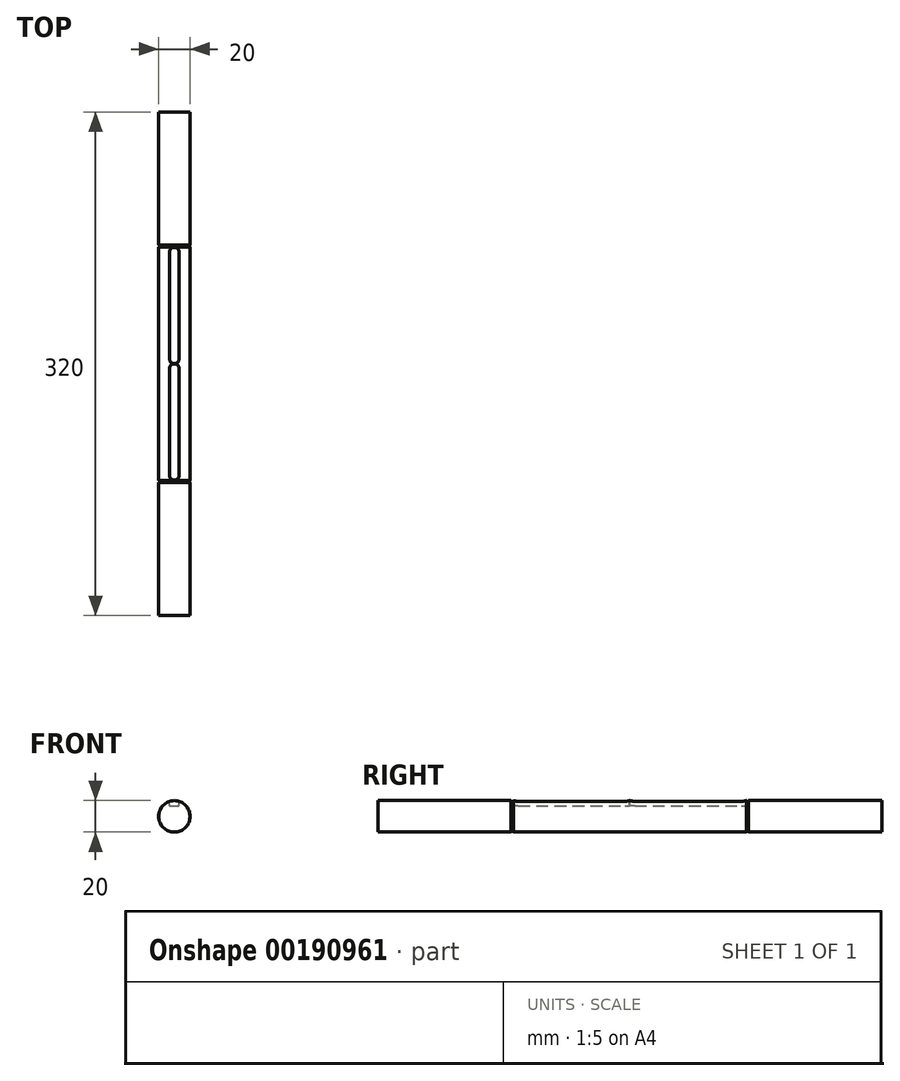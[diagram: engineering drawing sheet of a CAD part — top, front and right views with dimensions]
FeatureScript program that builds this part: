
annotation { "Feature Type Name" : "Feature", "Feature Type Description" : "" }
export const myFeature = defineFeature(function(context is Context, id is Id, definition is map)
    precondition{}
    {
        {
            var Q0;
            Q0=qCreatedBy(makeId("Front.planeOp"),FACE);
            var sketch = newSketch(context, id + "F0", { "sketchPlane" : qUnion([Q0])});
            skCircle(sketch, "E0", {"center": v(0, 0) * mm, "radius": 10 * mm});
            skSolve(sketch);
        }
        {
            var Q0;
            Q0=makeQuery(id+"F0.imprint","IMPRINT",FACE,{"disambiguationData":[TD([[makeQuery(id+"F0.imprint","IMPRINT",EDGE,{"derivedFrom":sQuery(id+"F0.wireOp",EDGE,"E0")}),1.0]])]});
            extrude(context, id + "F1", {"entities" : qUnion([Q0]), "depth" : 320 * mm});
        }
        {
            var Q0;
            Q0=qCreatedBy(makeId("Top.planeOp"),FACE);
            cPlane(context, id + "F2", {"entities" : qUnion([Q0]), "cplaneType" : CPlaneType.OFFSET, "offset" : 12.5 * mm, "width" : 150 * mm, "height" : 150 * mm});
        }
        {
            var Q0;
            Q0=qCreatedBy(id+"F2.planeOp",FACE);
            var sketch = newSketch(context, id + "F3", { "sketchPlane" : qUnion([Q0])});
            skLineSegment(sketch, "E1.bottom", {"start": v(-3, -230.9) * mm, "end": v(3, -230.9) * mm});
            skLineSegment(sketch, "E1.top", {"start": v(-3, -89.1) * mm, "end": v(3, -89.1) * mm});
            skLineSegment(sketch, "E1.left", {"start": v(-3, -230.9) * mm, "end": v(-3, -89.1) * mm});
            skLineSegment(sketch, "E1.right", {"start": v(3, -230.9) * mm, "end": v(3, -89.1) * mm});
            skArc(sketch, "E2", {"start": v(-3, -89.1) * mm, "mid": v(0, -86.1) * mm, "end": v(3, -89.1) * mm});
            skArc(sketch, "E3", {"start": v(3, -230.9) * mm, "mid": v(0, -233.9) * mm, "end": v(-3, -230.9) * mm});
            skCircle(sketch, "E4", {"center": v(0, -156.9) * mm, "radius": 3 * mm});
            skCircle(sketch, "E5", {"center": v(0, -163.1) * mm, "radius": 3 * mm});
            skSolve(sketch);
        }
        {
            var Q0;
            Q0=makeQuery(id+"F3.imprint","IMPRINT",FACE,{"disambiguationData":[TD([[makeQuery(id+"F3.imprint","IMPRINT",EDGE,{"derivedFrom":sQuery(id+"F3.wireOp",EDGE,"E1.bottom")}),1.0]])]});
            var Q1;
            Q1=makeQuery(id+"F3.imprint","IMPRINT",FACE,{"disambiguationData":[TD([[makeQuery(id+"F3.imprint","IMPRINT",EDGE,{"derivedFrom":sQuery(id+"F3.wireOp",EDGE,"E1.top")}),1.0]])]});
            var Q2;
            Q2=makeQuery(id+"F3.imprint","IMPRINT",FACE,{"disambiguationData":[TD([[makeQuery(id+"F3.imprint","IMPRINT",EDGE,{"derivedFrom":sQuery(id+"F3.wireOp",EDGE,"E1.bottom")}),-1.0]])]});
            var Q3;
            {var subQ0=sQuery(id+"F3.wireOp",EDGE,"E1.top");Q3=makeQuery(id+"F3.imprint","IMPRINT",FACE,{"disambiguationData":[TD([[makeQuery(id+"F3.imprint","IMPRINT",EDGE,{"derivedFrom":subQ0}),-1.0]])]});}
            var Q4;
            {var subQ0=sQuery(id+"F3.wireOp",EDGE,"E4");var subQ1=makeQuery(id+"F3.imprint","INTERSECT",VERTEX,{"derivedFrom":[sQuery(id+"F3.wireOp",EDGE,"E1.left"),subQ0]});Q4=makeQuery(id+"F3.imprint","IMPRINT",FACE,{"disambiguationData":[TD([[makeQuery(id+"F3.imprint","IMPRINT",EDGE,{"disambiguationData":[TD([[subQ1,1.0]])],"derivedFrom":subQ0}),1.0]])]});}
            var Q5;
            {var subQ0=sQuery(id+"F3.wireOp",EDGE,"E5");var subQ1=makeQuery(id+"F3.imprint","INTERSECT",VERTEX,{"derivedFrom":[sQuery(id+"F3.wireOp",EDGE,"E1.right"),subQ0]});Q5=makeQuery(id+"F3.imprint","IMPRINT",FACE,{"disambiguationData":[TD([[makeQuery(id+"F3.imprint","IMPRINT",EDGE,{"disambiguationData":[TD([[subQ1,-1.0]])],"derivedFrom":subQ0}),1.0]])]});}
            extrude(context, id + "F4", {"entities" : qUnion([Q0, Q1, Q2, Q3, Q4, Q5]), "operationType" : NewBodyOperationType.REMOVE, "oppositeDirection" : true, "depth" : 6 * mm});
        }
        {
            var Q0;
            Q0=qCreatedBy(makeId("Front.planeOp"),FACE);
            cPlane(context, id + "F5", {"entities" : qUnion([Q0]), "cplaneType" : CPlaneType.OFFSET, "offset" : 86 * mm, "width" : 150 * mm, "height" : 150 * mm});
        }
        {
            var Q0;
            Q0=qCreatedBy(id+"F5.planeOp",FACE);
            var sketch = newSketch(context, id + "F6", { "sketchPlane" : qUnion([Q0])});
            skCircle(sketch, "E6", {"center": v(0, 0) * mm, "radius": 10 * mm});
            skCircle(sketch, "E7", {"center": v(0, 0) * mm, "radius": 9.5 * mm});
            skSolve(sketch);
        }
        {
            var Q0;
            Q0 = qSketchRegion(id + "F6", true);
            extrude(context, id + "F7", {"entities" : qUnion([Q0]), "operationType" : NewBodyOperationType.REMOVE, "oppositeDirection" : true, "depth" : 1.35 * mm});
        }
        {
            var Q0;
            Q0=makeQuery(id+"F1.opExtrude","CAP_FACE",FACE,{"disambiguationData":[OSD([sQuery(id+"F0.wireOp",EDGE,"E0")])],"isStart":false});
            cPlane(context, id + "F8", {"entities" : qUnion([Q0]), "cplaneType" : CPlaneType.OFFSET, "offset" : 86 * mm, "oppositeDirection" : true, "width" : 150 * mm, "height" : 150 * mm});
        }
        {
            var Q0;
            Q0=qCreatedBy(id+"F8.planeOp",FACE);
            var sketch = newSketch(context, id + "F9", { "sketchPlane" : qUnion([Q0])});
            skCircle(sketch, "E8", {"center": v(0, 0) * mm, "radius": 10 * mm});
            skCircle(sketch, "E9", {"center": v(0, 0) * mm, "radius": 9.5 * mm});
            skSolve(sketch);
        }
        {
            var Q0;
            Q0 = qSketchRegion(id + "F9", true);
            extrude(context, id + "F10", {"entities" : qUnion([Q0]), "operationType" : NewBodyOperationType.REMOVE, "depth" : 1.35 * mm});
        }
    });
